# Revit family: IEK_Зажим соединительный круглого проводника_6-12мм
name_source: partatom
category: Обобщенные модели
units: mm (PartAtom-declared; Revit-internal decimal feet)

## family parameters
Может служить основой для арматурных стержней = Нет
Общий = Да
Основа = Грань
При загрузке вырезать с полостями = Нет
Размер круглого соединителя = Использовать диаметр
Тип детали = Нормальный
Точка расчета площади = Нет

## types (3) — shared parameters
ADSK_URL страницы изделия = https://www.iek.ru
ADSK_Версия Revit = 2019
ADSK_Версия семейства = 1.0
ADSK_Группирование = VIII. ЭЛЕМЕНТЫ ВНЕШНЕЙ МОЛНИЕЗАЩИТЫ
ADSK_Единица измерения = шт
ADSK_Завод-изготовитель = IEK
IEK_Описание = Универсальная конструкция зажима позволяет использовать его с проводниками различной формы и габаритами.
zero-valued in all types: Отметка по умолчанию

## per-type parameters (varying)
| type | ADSK_Код изделия | ADSK_Масса | ADSK_Материал | ADSK_Материал наименование | ADSK_Наименование | IEK_URL | IEK_Цена за единицу | KSI_CMa_Строительные материалы |
| 6-12_Сталь оцинкованная | ZCC80-11-1-16 | 0.08 | Сталь оцинкованная | Сталь оцинкованная | Зажим соединительный круглого проводника 6-12мм оцинкованная сталь IEK | https://www.iek.ru | 183.6 | 24.10.35.000.08.3.05.06-0001 |
| 6-12_Латунь | ZCC80-40-1-16 | 0.09 | Латунь | Латунь | Зажим соединительный круглого проводника 6-12мм латунь IEK |  | 602 | 10.2.01.02 |
| 6-12_Медь | ZCC80-50-1-16 | 0.09 | Медь | Медь | Зажим соединительный круглого проводника 6-12мм медь IEK |  | 1008 | 10.2.01.02 |

## geometry (parser evidence)
native form markers: Blend x2
no freeform markers — native parametric forms only
